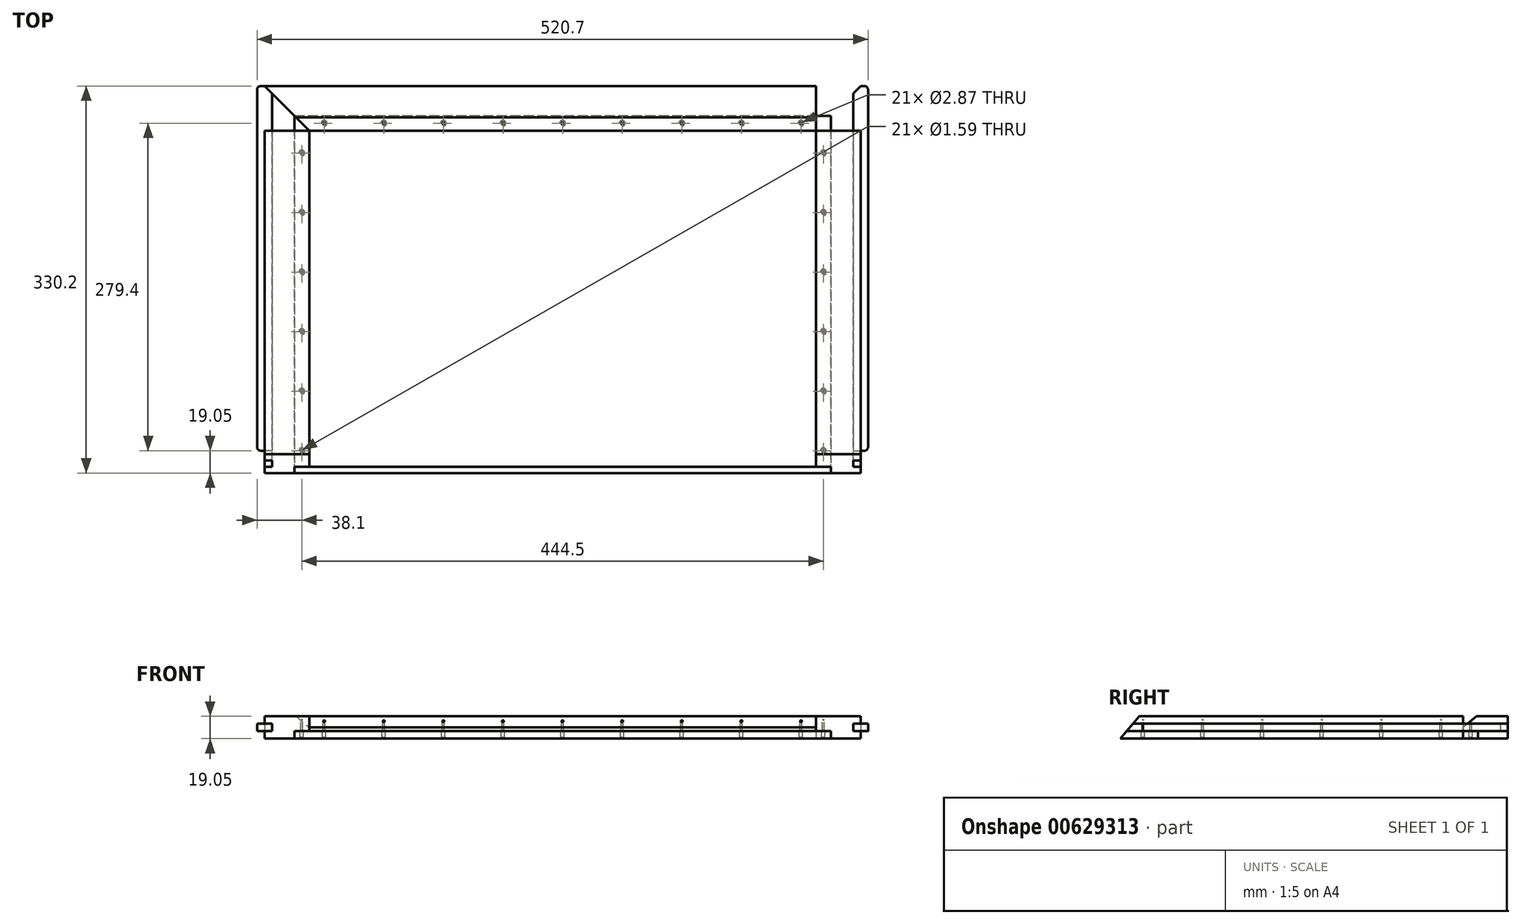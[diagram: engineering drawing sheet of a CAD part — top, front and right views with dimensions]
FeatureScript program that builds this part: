
annotation { "Feature Type Name" : "Feature", "Feature Type Description" : "" }
export const myFeature = defineFeature(function(context is Context, id is Id, definition is map)
    precondition{}
    {
        {
            var Q0;
            Q0=qCreatedBy(makeId("Right.planeOp"),FACE);
            var sketch = newSketch(context, id + "F0", { "sketchPlane" : qUnion([Q0])});
            skLineSegment(sketch, "E0.bottom", {"start": v(0, 0) * mm, "end": v(-25.4, 0) * mm});
            skLineSegment(sketch, "E0.top", {"start": v(0, 19.05) * mm, "end": v(-26.75, 19.05) * mm});
            skLineSegment(sketch, "E0.left", {"start": v(0, 0) * mm, "end": v(0, 19.05) * mm});
            skLineSegment(sketch, "E0.right", {"start": v(-38.1, 6.35) * mm, "end": v(-38.1, 9.52) * mm});
            skLineSegment(sketch, "E1.top", {"start": v(-38.1, 6.35) * mm, "end": v(-25.4, 6.35) * mm});
            skLineSegment(sketch, "E1.right", {"start": v(-25.4, 0) * mm, "end": v(-25.4, 6.35) * mm});
            skLineSegment(sketch, "E2", {"start": v(-38.1, 9.52) * mm, "end": v(-26.75, 19.05) * mm});
            skSolve(sketch);
        }
        {
            var Q0;
            Q0=makeQuery(id+"F0.imprint","IMPRINT",FACE,{"disambiguationData":[TD([[makeQuery(id+"F0.imprint","IMPRINT",EDGE,{"derivedFrom":sQuery(id+"F0.wireOp",EDGE,"E0.bottom")}),-1.0]])]});
            extrude(context, id + "F1", {"entities" : qUnion([Q0]), "depth" : 508 * mm, "offsetDistance" : 25.4 * mm, "symmetric" : true});
        }
        {
            var Q0;
            Q0=qCreatedBy(makeId("Front.planeOp"),FACE);
            var sketch = newSketch(context, id + "F2", { "sketchPlane" : qUnion([Q0])});
            skLineSegment(sketch, "E3.bottom", {"start": v(254, 0) * mm, "end": v(228.6, 0) * mm});
            skLineSegment(sketch, "E3.top", {"start": v(254, 19.05) * mm, "end": v(215.9, 19.05) * mm});
            skLineSegment(sketch, "E3.left", {"start": v(254, 0) * mm, "end": v(254, 6.35) * mm});
            skLineSegment(sketch, "E3.right", {"start": v(215.9, 6.35) * mm, "end": v(215.9, 19.05) * mm});
            skLineSegment(sketch, "E4.top", {"start": v(215.9, 6.35) * mm, "end": v(228.6, 6.35) * mm});
            skLineSegment(sketch, "E4.right", {"start": v(228.6, 0) * mm, "end": v(228.6, 6.35) * mm});
            skLineSegment(sketch, "E5.bottom", {"start": v(254, 6.35) * mm, "end": v(247.65, 6.35) * mm});
            skLineSegment(sketch, "E5.top", {"start": v(254, 12.7) * mm, "end": v(247.65, 12.7) * mm});
            skLineSegment(sketch, "E5.right", {"start": v(247.65, 6.35) * mm, "end": v(247.65, 12.7) * mm});
            skLineSegment(sketch, "E6.trimOffspring", {"start": v(254, 12.7) * mm, "end": v(254, 19.05) * mm});
            skSolve(sketch);
        }
        {
            var Q0;
            Q0 = qSketchRegion(id + "F2", true);
            extrude(context, id + "F3", {"entities" : qUnion([Q0]), "depth" : 330.2 * mm, "offsetDistance" : 25.4 * mm});
        }
        {
            var Q0;
            Q0=makeQuery(id+"F1.opExtrude","SWEPT_FACE",FACE,{"disambiguationData":[OSD([sQuery(id+"F0.wireOp",EDGE,"E0.top")])]});
            var sketch = newSketch(context, id + "F4", { "sketchPlane" : qUnion([Q0])});
            skLineSegment(sketch, "E7", {"start": v(254, 0) * mm, "end": v(215.9, -38.1) * mm});
            skLineSegment(sketch, "E8", {"start": v(254, 0) * mm, "end": v(254, -38.1) * mm});
            skLineSegment(sketch, "E9", {"start": v(254, -38.1) * mm, "end": v(215.9, -38.1) * mm});
            skSolve(sketch);
        }
        {
            var Q0;
            Q0 = qSketchRegion(id + "F4", true);
            extrude(context, id + "F5", {"entities" : qUnion([Q0]), "operationType" : NewBodyOperationType.REMOVE, "endBound" : BoundingType.THROUGH_ALL, "oppositeDirection" : true, "depth" : 25.4 * mm, "offsetDistance" : 25.4 * mm});
        }
        {
            var Q0;
            Q0=makeQuery(id+"F1.opExtrude","SWEPT_FACE",FACE,{"disambiguationData":[OSD([sQuery(id+"F0.wireOp",EDGE,"E0.top")])]});
            var sketch = newSketch(context, id + "F6", { "sketchPlane" : qUnion([Q0])});
            skLineSegment(sketch, "E10.top", {"start": v(-254, -38.1) * mm, "end": v(-215.9, -38.1) * mm});
            skLineSegment(sketch, "E10.left", {"start": v(-254, 0) * mm, "end": v(-254, -38.1) * mm});
            skLineSegment(sketch, "E11", {"start": v(-254, 0) * mm, "end": v(-215.9, -38.1) * mm});
            skSolve(sketch);
        }
        {
            var Q0;
            Q0 = qSketchRegion(id + "F6", true);
            extrude(context, id + "F7", {"entities" : qUnion([Q0]), "operationType" : NewBodyOperationType.REMOVE, "endBound" : BoundingType.THROUGH_ALL, "oppositeDirection" : true, "depth" : 25.4 * mm, "offsetDistance" : 25.4 * mm});
        }
        {
            var Q0;
            Q0=makeQuery(id+"F3.opExtrude","SWEPT_FACE",FACE,{"disambiguationData":[OSD([sQuery(id+"F2.wireOp",EDGE,"E3.top")])]});
            var sketch = newSketch(context, id + "F8", { "sketchPlane" : qUnion([Q0])});
            skLineSegment(sketch, "E12.bottom", {"start": v(254, 0) * mm, "end": v(215.9, 0) * mm});
            skLineSegment(sketch, "E12.right", {"start": v(215.9, 0) * mm, "end": v(215.9, -38.1) * mm});
            skLineSegment(sketch, "E13", {"start": v(215.9, -38.1) * mm, "end": v(254, 0) * mm});
            skSolve(sketch);
        }
        {
            var Q0;
            Q0 = qSketchRegion(id + "F8", true);
            extrude(context, id + "F9", {"entities" : qUnion([Q0]), "operationType" : NewBodyOperationType.REMOVE, "endBound" : BoundingType.THROUGH_ALL, "oppositeDirection" : true, "depth" : 25.4 * mm, "offsetDistance" : 25.4 * mm});
        }
        {
            var Q0;
            Q0=makeQuery(id+"F3.opExtrude","SWEPT_FACE",FACE,{"disambiguationData":[OSD([sQuery(id+"F2.wireOp",EDGE,"E6.trimOffspring")])]});
            var sketch = newSketch(context, id + "F10", { "sketchPlane" : qUnion([Q0])});
            skLineSegment(sketch, "E14.top", {"start": v(-330.2, 19.05) * mm, "end": v(-314.22, 19.05) * mm});
            skLineSegment(sketch, "E14.left", {"start": v(-330.2, 0) * mm, "end": v(-330.2, 19.05) * mm});
            skLineSegment(sketch, "E15", {"start": v(-330.2, 0) * mm, "end": v(-314.22, 19.05) * mm});
            skSolve(sketch);
        }
        {
            var Q0;
            Q0 = qSketchRegion(id + "F10", true);
            extrude(context, id + "F11", {"entities" : qUnion([Q0]), "operationType" : NewBodyOperationType.REMOVE, "endBound" : BoundingType.THROUGH_ALL, "oppositeDirection" : true, "depth" : 25.4 * mm, "offsetDistance" : 25.4 * mm});
        }
        {
            var Q0;
            Q0=makeQuery(id+"F3.opExtrude","SWEPT_BODY",BODY,{"disambiguationData":[OSD([sQuery(id+"F2.wireOp",EDGE,"E3.bottom"),sQuery(id+"F2.wireOp",EDGE,"E3.top"),sQuery(id+"F2.wireOp",EDGE,"E3.left"),sQuery(id+"F2.wireOp",EDGE,"E3.right"),sQuery(id+"F2.wireOp",EDGE,"E4.top"),sQuery(id+"F2.wireOp",EDGE,"E4.right"),sQuery(id+"F2.wireOp",EDGE,"E5.bottom"),sQuery(id+"F2.wireOp",EDGE,"E5.top"),sQuery(id+"F2.wireOp",EDGE,"E5.right"),sQuery(id+"F2.wireOp",EDGE,"E6.trimOffspring")])]});
            var Q1;
            Q1=qCreatedBy(makeId("Right.planeOp"),FACE);
            mirror(context, id + "F12", {"entities" : qUnion([Q0]), "mirrorPlane" : qUnion([Q1])});
        }
        {
            var Q0;
            Q0=makeQuery(id+"F1.opExtrude","SWEPT_FACE",FACE,{"disambiguationData":[OSD([sQuery(id+"F0.wireOp",EDGE,"E0.bottom")])]});
            var sketch = newSketch(context, id + "F13", { "sketchPlane" : qUnion([Q0])});
            skLineSegment(sketch, "E16.bottom", {"start": v(228.6, 25.4) * mm, "end": v(-228.6, 25.4) * mm});
            skLineSegment(sketch, "E16.top", {"start": v(228.6, 330.2) * mm, "end": v(-228.6, 330.2) * mm});
            skLineSegment(sketch, "E16.left", {"start": v(228.6, 25.4) * mm, "end": v(228.6, 330.2) * mm});
            skLineSegment(sketch, "E16.right", {"start": v(-228.6, 25.4) * mm, "end": v(-228.6, 330.2) * mm});
            skSolve(sketch);
        }
        {
            var Q0;
            Q0 = qSketchRegion(id + "F13", true);
            extrude(context, id + "F14", {"entities" : qUnion([Q0]), "oppositeDirection" : true, "depth" : 6.35 * mm, "offsetDistance" : 25.4 * mm});
        }
        {
            var Q0;
            Q0=makeQuery(id+"F14.opExtrude","SWEPT_FACE",FACE,{"disambiguationData":[OSD([sQuery(id+"F13.wireOp",EDGE,"E16.left")])]});
            var sketch = newSketch(context, id + "F15", { "sketchPlane" : qUnion([Q0])});
            skLineSegment(sketch, "E17", {"start": v(-330.2, 0) * mm, "end": v(-330.2, 6.35) * mm});
            skLineSegment(sketch, "E18", {"start": v(-330.2, 6.35) * mm, "end": v(-324.87, 6.35) * mm});
            skLineSegment(sketch, "E19", {"start": v(-324.87, 6.35) * mm, "end": v(-330.2, 0) * mm});
            skSolve(sketch);
        }
        {
            var Q0;
            Q0 = qSketchRegion(id + "F15", true);
            extrude(context, id + "F16", {"entities" : qUnion([Q0]), "operationType" : NewBodyOperationType.REMOVE, "endBound" : BoundingType.THROUGH_ALL, "oppositeDirection" : true, "depth" : 25.4 * mm, "offsetDistance" : 25.4 * mm});
        }
        {
            var Q0;
            Q0=makeQuery(id+"F12.opPattern","COPY",FACE,{"derivedFrom":makeQuery(id+"F3.opExtrude","SWEPT_FACE",FACE,{"disambiguationData":[OSD([sQuery(id+"F2.wireOp",EDGE,"E3.bottom")])]}),"instanceName":"1"});
            var sketch = newSketch(context, id + "F17", { "sketchPlane" : qUnion([Q0])});
            skLineSegment(sketch, "E20.0", {"start": v(222.25, 31.75) * mm, "end": v(222.25, 311.15) * mm});
            skLineSegment(sketch, "E21.0", {"start": v(-222.25, 31.75) * mm, "end": v(222.25, 31.75) * mm});
            skLineSegment(sketch, "E22.0", {"start": v(-222.25, 311.15) * mm, "end": v(-222.25, 31.75) * mm});
            skCircle(sketch, "E23", {"center": v(0, 31.75) * mm, "radius": 50.8 * mm, "construction": true});
            skCircle(sketch, "E24.0", {"center": v(0, 31.75) * mm, "radius": 101.6 * mm, "construction": true});
            skCircle(sketch, "E25.0", {"center": v(0, 31.75) * mm, "radius": 152.4 * mm, "construction": true});
            skLineSegment(sketch, "E26.0", {"start": v(-222.25, 285.75) * mm, "end": v(-222.25, 31.75) * mm, "construction": true});
            skLineSegment(sketch, "E26.2", {"start": v(222.25, 31.75) * mm, "end": v(222.25, 285.75) * mm, "construction": true});
            skLineSegment(sketch, "E26.3", {"start": v(-222.25, 31.75) * mm, "end": v(222.25, 31.75) * mm, "construction": true});
            skCircle(sketch, "E27.0", {"center": v(0, 31.75) * mm, "radius": 203.2 * mm, "construction": true});
            skCircle(sketch, "E28", {"center": v(222.25, 31.75) * mm, "radius": 25.4 * mm, "construction": true});
            skCircle(sketch, "E29.0", {"center": v(222.25, 31.75) * mm, "radius": 76.2 * mm, "construction": true});
            skCircle(sketch, "E30.0", {"center": v(222.25, 31.75) * mm, "radius": 127 * mm, "construction": true});
            skCircle(sketch, "E31.0", {"center": v(222.25, 31.75) * mm, "radius": 177.8 * mm, "construction": true});
            skCircle(sketch, "E32.0", {"center": v(222.25, 31.75) * mm, "radius": 228.6 * mm, "construction": true});
            skCircle(sketch, "E33.MirrorC", {"center": v(-222.25, 31.75) * mm, "radius": 25.4 * mm, "construction": true});
            skCircle(sketch, "E34.MirrorC", {"center": v(-222.25, 31.75) * mm, "radius": 76.2 * mm, "construction": true});
            skCircle(sketch, "E35.MirrorC", {"center": v(-222.25, 31.75) * mm, "radius": 228.6 * mm, "construction": true});
            skCircle(sketch, "E36.MirrorC", {"center": v(-222.25, 31.75) * mm, "radius": 177.8 * mm, "construction": true});
            skCircle(sketch, "E37.MirrorC", {"center": v(-222.25, 31.75) * mm, "radius": 127 * mm, "construction": true});
            skPoint(sketch, "E38", {"position": v(-222.25, 260.35) * mm});
            skPoint(sketch, "E39", {"position": v(-222.25, 209.55) * mm});
            skPoint(sketch, "E40", {"position": v(-222.25, 158.75) * mm});
            skPoint(sketch, "E41", {"position": v(-222.25, 107.95) * mm});
            skPoint(sketch, "E42", {"position": v(-222.25, 57.15) * mm});
            skPoint(sketch, "E43", {"position": v(222.25, 260.35) * mm});
            skPoint(sketch, "E44", {"position": v(222.25, 209.55) * mm});
            skPoint(sketch, "E45", {"position": v(222.25, 158.75) * mm});
            skPoint(sketch, "E46", {"position": v(222.25, 107.95) * mm});
            skPoint(sketch, "E47", {"position": v(222.25, 57.15) * mm});
            skPoint(sketch, "E48", {"position": v(203.2, 31.75) * mm});
            skPoint(sketch, "E49", {"position": v(152.4, 31.75) * mm});
            skPoint(sketch, "E50", {"position": v(101.6, 31.75) * mm});
            skPoint(sketch, "E51", {"position": v(50.8, 31.75) * mm});
            skPoint(sketch, "E52", {"position": v(-50.8, 31.75) * mm});
            skPoint(sketch, "E53", {"position": v(-101.6, 31.75) * mm});
            skPoint(sketch, "E54", {"position": v(-152.4, 31.75) * mm});
            skPoint(sketch, "E55", {"position": v(-203.2, 31.75) * mm});
            skCircle(sketch, "E56.0", {"center": v(222.25, 31.75) * mm, "radius": 279.4 * mm});
            skCircle(sketch, "E57.0", {"center": v(-222.25, 31.75) * mm, "radius": 279.4 * mm});
            skPoint(sketch, "E58", {"position": v(222.25, 311.15) * mm});
            skPoint(sketch, "E59", {"position": v(-222.25, 311.15) * mm});
            skSolve(sketch);
        }
        {
            var Q0;
            Q0=sQuery(id+"F17.wireOp",VERTEX,"E43");
            var Q1;
            Q1=sQuery(id+"F17.wireOp",VERTEX,"E44");
            var Q2;
            Q2=sQuery(id+"F17.wireOp",VERTEX,"E45");
            var Q3;
            Q3=sQuery(id+"F17.wireOp",VERTEX,"E46");
            var Q4;
            Q4=sQuery(id+"F17.wireOp",VERTEX,"E47");
            var Q5;
            Q5=sQuery(id+"F17.wireOp",VERTEX,"E58");
            var Q6;
            Q6=makeQuery(id+"F3.opExtrude","SWEPT_BODY",BODY,{"disambiguationData":[OSD([sQuery(id+"F2.wireOp",EDGE,"E3.bottom"),sQuery(id+"F2.wireOp",EDGE,"E3.top"),sQuery(id+"F2.wireOp",EDGE,"E3.left"),sQuery(id+"F2.wireOp",EDGE,"E3.right"),sQuery(id+"F2.wireOp",EDGE,"E4.top"),sQuery(id+"F2.wireOp",EDGE,"E4.right"),sQuery(id+"F2.wireOp",EDGE,"E5.bottom"),sQuery(id+"F2.wireOp",EDGE,"E5.top"),sQuery(id+"F2.wireOp",EDGE,"E5.right"),sQuery(id+"F2.wireOp",EDGE,"E6.trimOffspring")])]});
            var Q7;
            Q7=makeQuery(id+"F14.opExtrude","SWEPT_BODY",BODY,{"disambiguationData":[OSD([sQuery(id+"F13.wireOp",EDGE,"E16.bottom"),sQuery(id+"F13.wireOp",EDGE,"E16.top"),sQuery(id+"F13.wireOp",EDGE,"E16.left"),sQuery(id+"F13.wireOp",EDGE,"E16.right")])]});
            hole(context, id + "F18", {"style" : HoleStyle.SIMPLE, "endStyle" : HoleEndStyle.BLIND, "holeDiameter" : 1.59 * mm, "majorDiameter" : 6.35 * mm, "holeDepth" : 15.88 * mm, "isTappedThrough" : true, "tappedDepth" : 12.7 * mm, "tapClearance" : 3, "locations" : qUnion([Q0, Q1, Q2, Q3, Q4, Q5]), "scope" : qUnion([Q6, Q7]), "startStyle" : HoleStartStyle.PART});
        }
        {
            var Q0;
            Q0=sQuery(id+"F17.wireOp",VERTEX,"E38");
            var Q1;
            Q1=sQuery(id+"F17.wireOp",VERTEX,"E39");
            var Q2;
            Q2=sQuery(id+"F17.wireOp",VERTEX,"E40");
            var Q3;
            Q3=sQuery(id+"F17.wireOp",VERTEX,"E42");
            var Q4;
            Q4=sQuery(id+"F17.wireOp",VERTEX,"E41");
            var Q5;
            Q5=sQuery(id+"F17.wireOp",VERTEX,"E59");
            var Q6;
            Q6=makeQuery(id+"F12.opPattern","COPY",BODY,{"derivedFrom":makeQuery(id+"F3.opExtrude","SWEPT_BODY",BODY,{"disambiguationData":[OSD([sQuery(id+"F2.wireOp",EDGE,"E3.bottom"),sQuery(id+"F2.wireOp",EDGE,"E3.top"),sQuery(id+"F2.wireOp",EDGE,"E3.left"),sQuery(id+"F2.wireOp",EDGE,"E3.right"),sQuery(id+"F2.wireOp",EDGE,"E4.top"),sQuery(id+"F2.wireOp",EDGE,"E4.right"),sQuery(id+"F2.wireOp",EDGE,"E5.bottom"),sQuery(id+"F2.wireOp",EDGE,"E5.top"),sQuery(id+"F2.wireOp",EDGE,"E5.right"),sQuery(id+"F2.wireOp",EDGE,"E6.trimOffspring")])]}),"instanceName":"1"});
            var Q7;
            Q7=makeQuery(id+"F14.opExtrude","SWEPT_BODY",BODY,{"disambiguationData":[OSD([sQuery(id+"F13.wireOp",EDGE,"E16.bottom"),sQuery(id+"F13.wireOp",EDGE,"E16.top"),sQuery(id+"F13.wireOp",EDGE,"E16.left"),sQuery(id+"F13.wireOp",EDGE,"E16.right")])]});
            hole(context, id + "F19", {"style" : HoleStyle.SIMPLE, "endStyle" : HoleEndStyle.BLIND, "holeDiameter" : 1.59 * mm, "majorDiameter" : 6.35 * mm, "holeDepth" : 15.88 * mm, "isTappedThrough" : true, "tappedDepth" : 12.7 * mm, "tapClearance" : 3, "locations" : qUnion([Q0, Q1, Q2, Q3, Q4, Q5]), "scope" : qUnion([Q6, Q7]), "startStyle" : HoleStartStyle.PART});
        }
        {
            var Q0;
            Q0=sQuery(id+"F17.wireOp",VERTEX,"E55");
            var Q1;
            Q1=sQuery(id+"F17.wireOp",VERTEX,"E54");
            var Q2;
            Q2=sQuery(id+"F17.wireOp",VERTEX,"E53");
            var Q3;
            Q3=sQuery(id+"F17.wireOp",VERTEX,"E52");
            var Q4;
            Q4=sQuery(id+"F17.wireOp",VERTEX,"E23.center");
            var Q5;
            Q5=sQuery(id+"F17.wireOp",VERTEX,"E51");
            var Q6;
            Q6=sQuery(id+"F17.wireOp",VERTEX,"E50");
            var Q7;
            Q7=sQuery(id+"F17.wireOp",VERTEX,"E49");
            var Q8;
            Q8=sQuery(id+"F17.wireOp",VERTEX,"E48");
            var Q9;
            Q9=makeQuery(id+"F1.opExtrude","SWEPT_BODY",BODY,{"disambiguationData":[OSD([sQuery(id+"F0.wireOp",EDGE,"E0.bottom"),sQuery(id+"F0.wireOp",EDGE,"E0.top"),sQuery(id+"F0.wireOp",EDGE,"E0.left"),sQuery(id+"F0.wireOp",EDGE,"E0.right"),sQuery(id+"F0.wireOp",EDGE,"E1.top"),sQuery(id+"F0.wireOp",EDGE,"E1.right"),sQuery(id+"F0.wireOp",EDGE,"E2")])]});
            var Q10;
            Q10=makeQuery(id+"F14.opExtrude","SWEPT_BODY",BODY,{"disambiguationData":[OSD([sQuery(id+"F13.wireOp",EDGE,"E16.bottom"),sQuery(id+"F13.wireOp",EDGE,"E16.top"),sQuery(id+"F13.wireOp",EDGE,"E16.left"),sQuery(id+"F13.wireOp",EDGE,"E16.right")])]});
            hole(context, id + "F20", {"style" : HoleStyle.SIMPLE, "endStyle" : HoleEndStyle.BLIND, "holeDiameter" : 1.59 * mm, "majorDiameter" : 6.35 * mm, "holeDepth" : 15.88 * mm, "isTappedThrough" : true, "tappedDepth" : 12.7 * mm, "tapClearance" : 3, "locations" : qUnion([Q0, Q1, Q2, Q3, Q4, Q5, Q6, Q7, Q8]), "scope" : qUnion([Q9, Q10]), "startStyle" : HoleStartStyle.PART});
        }
        {
            var Q0;
            Q0=sQuery(id+"F17.wireOp",VERTEX,"E38");
            var Q1;
            Q1=sQuery(id+"F17.wireOp",VERTEX,"E39");
            var Q2;
            Q2=sQuery(id+"F17.wireOp",VERTEX,"E40");
            var Q3;
            Q3=sQuery(id+"F17.wireOp",VERTEX,"E41");
            var Q4;
            Q4=sQuery(id+"F17.wireOp",VERTEX,"E42");
            var Q5;
            Q5=sQuery(id+"F17.wireOp",VERTEX,"E55");
            var Q6;
            Q6=sQuery(id+"F17.wireOp",VERTEX,"E54");
            var Q7;
            Q7=sQuery(id+"F17.wireOp",VERTEX,"E53");
            var Q8;
            Q8=sQuery(id+"F17.wireOp",VERTEX,"E52");
            var Q9;
            Q9=sQuery(id+"F17.wireOp",VERTEX,"E23.center");
            var Q10;
            Q10=sQuery(id+"F17.wireOp",VERTEX,"E51");
            var Q11;
            Q11=sQuery(id+"F17.wireOp",VERTEX,"E50");
            var Q12;
            Q12=sQuery(id+"F17.wireOp",VERTEX,"E49");
            var Q13;
            Q13=sQuery(id+"F17.wireOp",VERTEX,"E48");
            var Q14;
            Q14=sQuery(id+"F17.wireOp",VERTEX,"E47");
            var Q15;
            Q15=sQuery(id+"F17.wireOp",VERTEX,"E46");
            var Q16;
            Q16=sQuery(id+"F17.wireOp",VERTEX,"E45");
            var Q17;
            Q17=sQuery(id+"F17.wireOp",VERTEX,"E44");
            var Q18;
            Q18=sQuery(id+"F17.wireOp",VERTEX,"E43");
            var Q19;
            Q19=sQuery(id+"F17.wireOp",VERTEX,"E59");
            var Q20;
            Q20=sQuery(id+"F17.wireOp",VERTEX,"E58");
            var Q21;
            Q21=makeQuery(id+"F1.opExtrude","SWEPT_BODY",BODY,{"disambiguationData":[OSD([sQuery(id+"F0.wireOp",EDGE,"E0.bottom"),sQuery(id+"F0.wireOp",EDGE,"E0.top"),sQuery(id+"F0.wireOp",EDGE,"E0.left"),sQuery(id+"F0.wireOp",EDGE,"E0.right"),sQuery(id+"F0.wireOp",EDGE,"E1.top"),sQuery(id+"F0.wireOp",EDGE,"E1.right"),sQuery(id+"F0.wireOp",EDGE,"E2")])]});
            var Q22;
            Q22=makeQuery(id+"F3.opExtrude","SWEPT_BODY",BODY,{"disambiguationData":[OSD([sQuery(id+"F2.wireOp",EDGE,"E3.bottom"),sQuery(id+"F2.wireOp",EDGE,"E3.top"),sQuery(id+"F2.wireOp",EDGE,"E3.left"),sQuery(id+"F2.wireOp",EDGE,"E3.right"),sQuery(id+"F2.wireOp",EDGE,"E4.top"),sQuery(id+"F2.wireOp",EDGE,"E4.right"),sQuery(id+"F2.wireOp",EDGE,"E5.bottom"),sQuery(id+"F2.wireOp",EDGE,"E5.top"),sQuery(id+"F2.wireOp",EDGE,"E5.right"),sQuery(id+"F2.wireOp",EDGE,"E6.trimOffspring")])]});
            var Q23;
            Q23=makeQuery(id+"F12.opPattern","COPY",BODY,{"derivedFrom":makeQuery(id+"F3.opExtrude","SWEPT_BODY",BODY,{"disambiguationData":[OSD([sQuery(id+"F2.wireOp",EDGE,"E3.bottom"),sQuery(id+"F2.wireOp",EDGE,"E3.top"),sQuery(id+"F2.wireOp",EDGE,"E3.left"),sQuery(id+"F2.wireOp",EDGE,"E3.right"),sQuery(id+"F2.wireOp",EDGE,"E4.top"),sQuery(id+"F2.wireOp",EDGE,"E4.right"),sQuery(id+"F2.wireOp",EDGE,"E5.bottom"),sQuery(id+"F2.wireOp",EDGE,"E5.top"),sQuery(id+"F2.wireOp",EDGE,"E5.right"),sQuery(id+"F2.wireOp",EDGE,"E6.trimOffspring")])]}),"instanceName":"1"});
            var Q24;
            Q24=makeQuery(id+"F14.opExtrude","SWEPT_BODY",BODY,{"disambiguationData":[OSD([sQuery(id+"F13.wireOp",EDGE,"E16.bottom"),sQuery(id+"F13.wireOp",EDGE,"E16.top"),sQuery(id+"F13.wireOp",EDGE,"E16.left"),sQuery(id+"F13.wireOp",EDGE,"E16.right")])]});
            hole(context, id + "F21", {"style" : HoleStyle.C_SINK, "endStyle" : HoleEndStyle.BLIND, "holeDiameter" : 2.87 * mm, "cSinkDiameter" : 4.95 * mm, "cSinkAngle" : 82 * degree, "majorDiameter" : 6.35 * mm, "holeDepth" : 6.35 * mm, "isTappedThrough" : true, "tappedDepth" : 12.7 * mm, "tapClearance" : 3, "locations" : qUnion([Q0, Q1, Q2, Q3, Q4, Q5, Q6, Q7, Q8, Q9, Q10, Q11, Q12, Q13, Q14, Q15, Q16, Q17, Q18, Q19, Q20]), "scope" : qUnion([Q21, Q22, Q23, Q24]), "startStyle" : HoleStartStyle.SKETCH});
        }
        {
            var Q0;
            Q0=makeQuery(id+"F3.opExtrude","SWEPT_FACE",FACE,{"disambiguationData":[OSD([sQuery(id+"F2.wireOp",EDGE,"E5.bottom")])]});
            var sketch = newSketch(context, id + "F22", { "sketchPlane" : qUnion([Q0])});
            skLineSegment(sketch, "E60.top", {"start": v(247.65, -311.15) * mm, "end": v(260.35, -311.15) * mm});
            skLineSegment(sketch, "E60.left", {"start": v(247.65, -6.35) * mm, "end": v(247.65, -311.15) * mm});
            skLineSegment(sketch, "E60.right", {"start": v(260.35, -6.35) * mm, "end": v(260.35, -311.15) * mm});
            skLineSegment(sketch, "E61", {"start": v(247.65, -6.35) * mm, "end": v(254, 0) * mm});
            skLineSegment(sketch, "E62", {"start": v(254, 0) * mm, "end": v(260.35, 0) * mm});
            skLineSegment(sketch, "E63", {"start": v(260.35, -6.35) * mm, "end": v(260.35, 0) * mm});
            skSolve(sketch);
        }
        {
            var Q0;
            Q0 = qSketchRegion(id + "F22", true);
            extrude(context, id + "F23", {"entities" : qUnion([Q0]), "depth" : 6.35 * mm, "offsetDistance" : 25.4 * mm});
        }
        {
            var Q0;
            Q0=makeQuery(id+"F23.opExtrude","SWEPT_EDGE",EDGE,{"disambiguationData":[OSD([sQuery(id+"F22.wireOp",EDGE,"E60.top"),sQuery(id+"F22.wireOp",EDGE,"E60.right")])]});
            var Q1;
            Q1=makeQuery(id+"F23.opExtrude","SWEPT_EDGE",EDGE,{"disambiguationData":[OSD([sQuery(id+"F22.wireOp",EDGE,"E62"),sQuery(id+"F22.wireOp",EDGE,"E63")])]});
            fillet(context, id + "F24", {"entities" : qUnion([Q0, Q1]), "radius" : 3.17 * mm, "tangentPropagation" : true, "allowEdgeOverflow" : false});
        }
        {
            var Q0;
            Q0=makeQuery(id+"F23.opExtrude","SWEPT_BODY",BODY,{"disambiguationData":[OSD([sQuery(id+"F22.wireOp",EDGE,"E60.top"),sQuery(id+"F22.wireOp",EDGE,"E60.left"),sQuery(id+"F22.wireOp",EDGE,"E60.right"),sQuery(id+"F22.wireOp",EDGE,"E61"),sQuery(id+"F22.wireOp",EDGE,"E62"),sQuery(id+"F22.wireOp",EDGE,"E63")])]});
            var Q1;
            Q1=qCreatedBy(makeId("Right.planeOp"),FACE);
            mirror(context, id + "F25", {"entities" : qUnion([Q0]), "mirrorPlane" : qUnion([Q1])});
        }
    });
